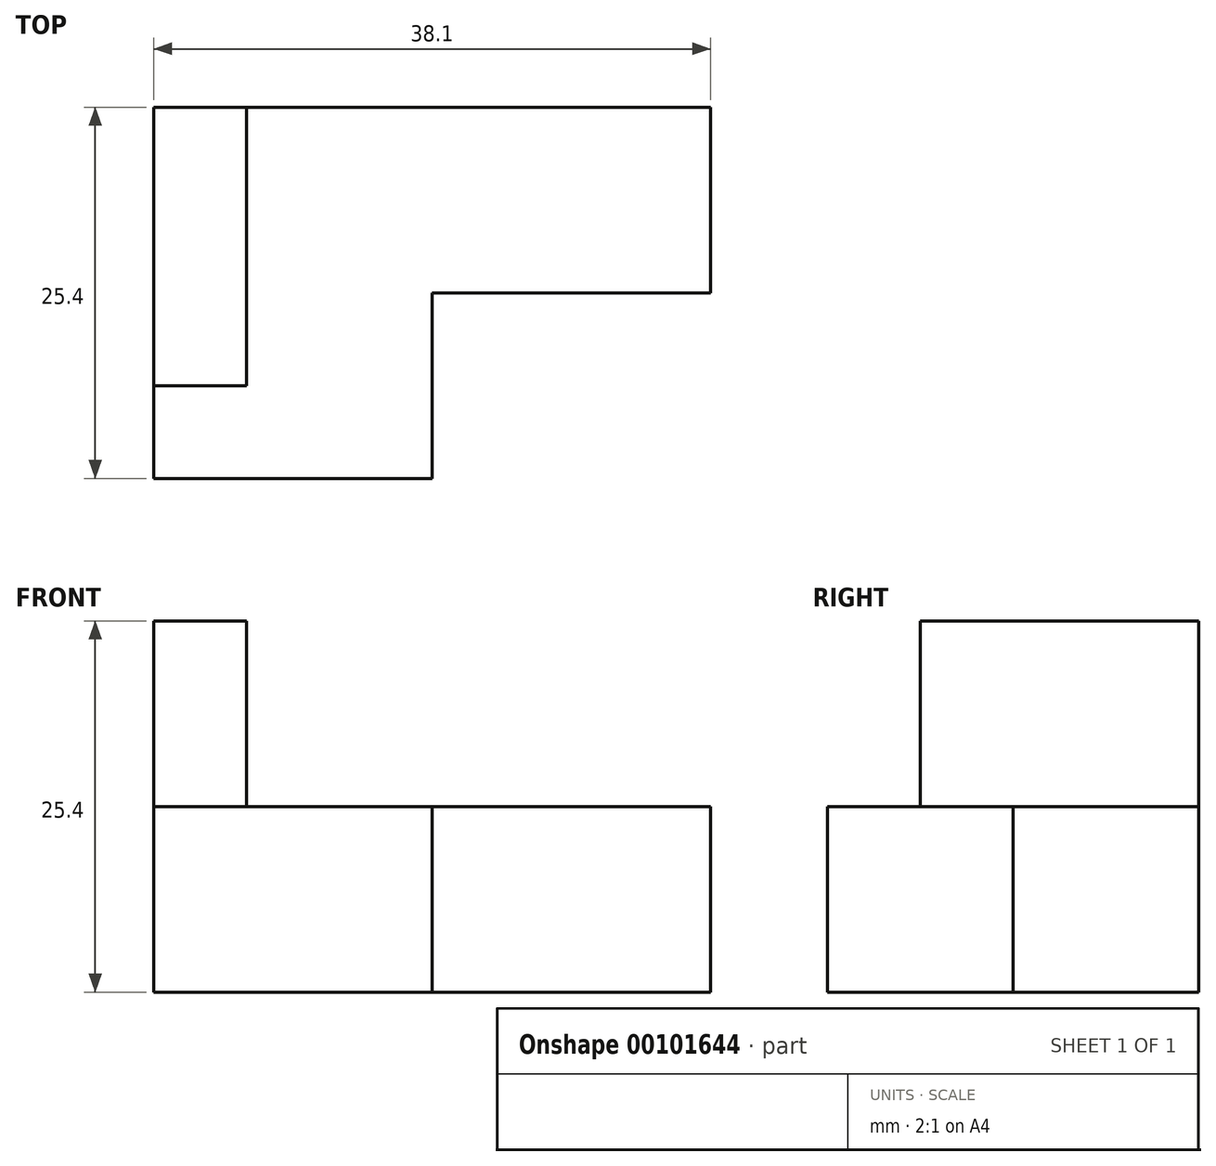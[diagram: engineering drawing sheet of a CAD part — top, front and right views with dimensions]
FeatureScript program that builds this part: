
annotation { "Feature Type Name" : "Feature", "Feature Type Description" : "" }
export const myFeature = defineFeature(function(context is Context, id is Id, definition is map)
    precondition{}
    {
        {
            var Q0;
            Q0=qCreatedBy(makeId("Top.planeOp"),FACE);
            var sketch = newSketch(context, id + "F0", { "sketchPlane" : qUnion([Q0])});
            skLineSegment(sketch, "E0", {"start": v(0, 0) * mm, "end": v(19.05, 0) * mm});
            skLineSegment(sketch, "E1", {"start": v(19.05, 0) * mm, "end": v(19.05, 12.7) * mm});
            skLineSegment(sketch, "E2", {"start": v(19.05, 12.7) * mm, "end": v(38.1, 12.7) * mm});
            skLineSegment(sketch, "E3", {"start": v(38.1, 12.7) * mm, "end": v(38.1, 25.4) * mm});
            skLineSegment(sketch, "E4", {"start": v(38.1, 25.4) * mm, "end": v(0, 25.4) * mm});
            skLineSegment(sketch, "E5", {"start": v(0, 25.4) * mm, "end": v(0, 0) * mm});
            skLineSegment(sketch, "E6", {"start": v(0, 6.35) * mm, "end": v(6.35, 6.35) * mm});
            skLineSegment(sketch, "E7", {"start": v(6.35, 6.35) * mm, "end": v(6.35, 25.4) * mm});
            skSolve(sketch);
        }
        {
            var Q0;
            {var subQ4=sQuery(id+"F0.wireOp",EDGE,"E6");Q0=makeQuery(id+"F0.imprint","IMPRINT",FACE,{"disambiguationData":[TD([[makeQuery(id+"F0.imprint","IMPRINT",EDGE,{"derivedFrom":subQ4}),1.0]])]});}
            extrude(context, id + "F1", {"entities" : qUnion([Q0]), "depth" : 25.4 * mm});
        }
        {
            var Q0;
            Q0 = qSketchRegion(id + "F0", true);
            extrude(context, id + "F2", {"entities" : qUnion([Q0]), "operationType" : NewBodyOperationType.ADD, "depth" : 12.7 * mm});
        }
    });
